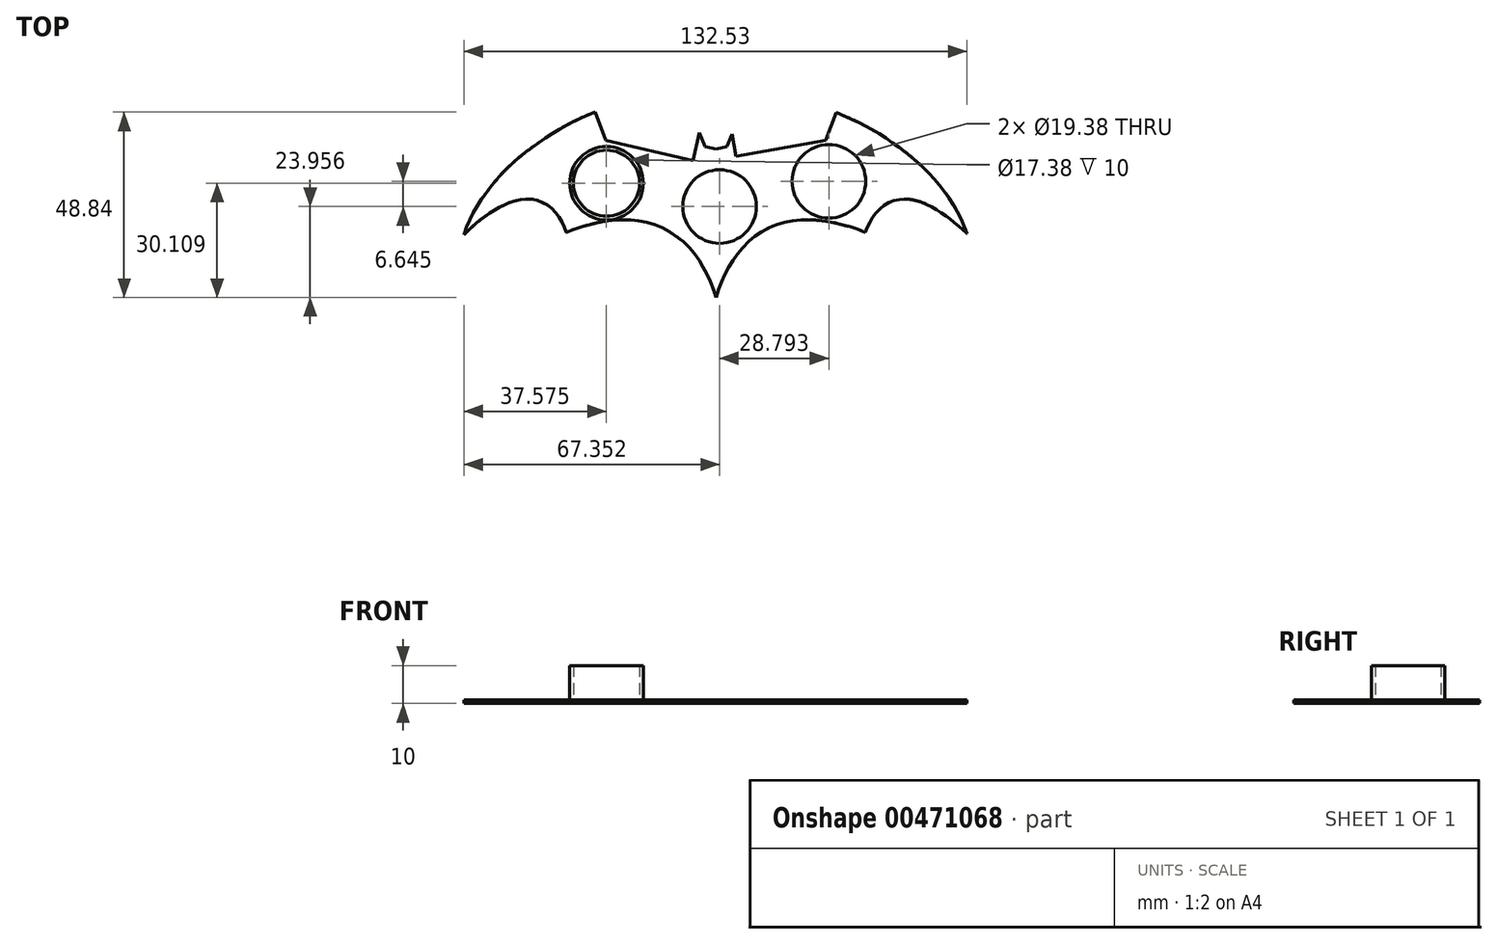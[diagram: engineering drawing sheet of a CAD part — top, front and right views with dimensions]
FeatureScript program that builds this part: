
annotation { "Feature Type Name" : "Feature", "Feature Type Description" : "" }
export const myFeature = defineFeature(function(context is Context, id is Id, definition is map)
    precondition{}
    {
        {
            var Q0;
            Q0=qCreatedBy(makeId("Top.planeOp"),FACE);
            var sketch = newSketch(context, id + "F0", { "sketchPlane" : qUnion([Q0])});
            skLineSegment(sketch, "E0", {"start": v(-31.58, 24.26) * mm, "end": v(-10.03, 19.27) * mm});
            skLineSegment(sketch, "E1", {"start": v(-8, 28.59) * mm, "end": v(-10.03, 19.27) * mm});
            skLineSegment(sketch, "E2", {"start": v(-8, 28.59) * mm, "end": v(-5.4, 22.6) * mm});
            skLineSegment(sketch, "E3", {"start": v(-5.4, 22.6) * mm, "end": v(-3.26, 22.12) * mm});
            skLineSegment(sketch, "E4", {"start": v(-3.26, 22.12) * mm, "end": v(-1.17, 22.6) * mm});
            skLineSegment(sketch, "E5", {"start": v(-1.17, 22.6) * mm, "end": v(1.35, 28.42) * mm});
            skLineSegment(sketch, "E6", {"start": v(1.35, 28.42) * mm, "end": v(2.82, 20.29) * mm});
            skLineSegment(sketch, "E7", {"start": v(2.82, 20.29) * mm, "end": v(24.86, 24.27) * mm});
            skLineSegment(sketch, "E8", {"start": v(24.86, 24.27) * mm, "end": v(27.86, 32.06) * mm});
            skLineSegment(sketch, "E9", {"start": v(-34.44, 32.06) * mm, "end": v(-31.58, 24.26) * mm});
            skFitSpline(sketch, "E10", {"points": [v(-71.54, -4.71) * mm, v(-71.03, -2.5) * mm, v(-69.95, 0.68) * mm, v(-67.87, 5.16) * mm, v(-64.53, 10.23) * mm, v(-59.84, 15.82) * mm, v(-53.37, 21.52) * mm, v(-43.46, 28) * mm, v(-34.44, 32.06) * mm], "startDerivative": vector(4.24, 29.82) * mm, "endDerivative": vector(55.88, 18.78) * mm});
            skFitSpline(sketch, "E11", {"points": [v(27.86, 32.06) * mm, v(37.3, 27.63) * mm, v(49.63, 19.06) * mm, v(56.76, 11.65) * mm, v(62.35, 2.73) * mm, v(64.86, -4.31) * mm, v(64.94, -4.74) * mm], "startDerivative": vector(44.14, -20.82) * mm, "endDerivative": vector(-0.74, -4.48) * mm});
            skFitSpline(sketch, "E12", {"points": [v(-3.32, -22.53) * mm, v(-2.72, -19.76) * mm, v(-1.9, -16.94) * mm, v(-0.8, -14.08) * mm, v(0.62, -11.17) * mm, v(2.24, -8.43) * mm, v(4.47, -5.7) * mm, v(6.98, -3.2) * mm, v(10.55, -0.92) * mm, v(13.84, 0.47) * mm, v(17.74, 1.21) * mm, v(20.5, 1.43) * mm, v(24.05, 1.25) * mm, v(27.15, 0.8) * mm, v(30.17, 0) * mm, v(32.95, -0.73) * mm, v(35, -1.57) * mm, v(36.1, -1.99) * mm, v(36.74, -2.23) * mm], "startDerivative": vector(8.47, 52.94) * mm, "endDerivative": vector(22.36, -9.6) * mm});
            skFitSpline(sketch, "E13", {"points": [v(36.74, -2.23) * mm, v(37.05, -1.12) * mm, v(37.6, 0.23) * mm, v(38.25, 1.59) * mm, v(39.23, 3.06) * mm, v(40.4, 4.38) * mm, v(41.46, 5.31) * mm, v(43.24, 6.28) * mm, v(44.9, 6.7) * mm, v(46.68, 6.86) * mm, v(48.66, 6.61) * mm, v(50.93, 5.93) * mm, v(52.85, 5.01) * mm, v(54.3, 4.22) * mm, v(56.14, 3) * mm, v(57.65, 1.91) * mm, v(59.33, 0.53) * mm, v(60.65, -0.55) * mm, v(62.13, -1.93) * mm, v(63.66, -3.41) * mm, v(64.95, -4.78) * mm, v(64.94, -4.74) * mm], "startDerivative": vector(6.9, 27.44) * mm, "endDerivative": vector(-2.9, -4.8) * mm});
            skFitSpline(sketch, "E14", {"points": [v(-43.33, -2.18) * mm, v(-41.74, -1.52) * mm, v(-38.77, -0.52) * mm, v(-35.27, 0.45) * mm, v(-31.24, 1.23) * mm, v(-28, 1.42) * mm, v(-24.68, 1.3) * mm, v(-21.72, 0.73) * mm, v(-19.2, 0) * mm, v(-16.85, -1.17) * mm, v(-14.55, -2.63) * mm, v(-12.25, -4.36) * mm, v(-10.35, -6.38) * mm, v(-8.73, -8.5) * mm, v(-6.94, -11.64) * mm, v(-5.72, -14.16) * mm, v(-4.63, -17.16) * mm, v(-3.93, -19.46) * mm, v(-3.32, -22.53) * mm], "startDerivative": vector(35.49, 10.52) * mm, "endDerivative": vector(12.6, -55.15) * mm});
            skFitSpline(sketch, "E15", {"points": [v(-71.54, -4.71) * mm, v(-70.46, -3.6) * mm, v(-68.76, -2.05) * mm, v(-66.86, -0.23) * mm, v(-65, 1.37) * mm, v(-62.35, 3.3) * mm, v(-60.63, 4.38) * mm, v(-58.87, 5.33) * mm, v(-57.1, 6.08) * mm, v(-55.15, 6.61) * mm, v(-53.48, 6.83) * mm, v(-51.43, 6.77) * mm, v(-50.1, 6.4) * mm, v(-48.82, 5.81) * mm, v(-47.8, 5.17) * mm, v(-46.87, 4.33) * mm, v(-46.13, 3.5) * mm, v(-45.4, 2.43) * mm, v(-44.7, 1.23) * mm, v(-44.2, 0.34) * mm, v(-43.79, -0.9) * mm, v(-43.47, -1.78) * mm, v(-43.33, -2.18) * mm], "startDerivative": vector(22.6, 24.07) * mm, "endDerivative": vector(5.32, -15.58) * mm});
            skCircle(sketch, "E16", {"center": v(26.46, 12.55) * mm, "radius": 8.7 * mm});
            skCircle(sketch, "E17", {"center": v(-2.34, 5.9) * mm, "radius": 8.7 * mm});
            skCircle(sketch, "E18", {"center": v(-32.12, 12.06) * mm, "radius": 8.7 * mm});
            skSolve(sketch);
        }
        {
            var Q0;
            Q0=makeQuery(id+"F0.imprint","IMPRINT",FACE,{"disambiguationData":[TD([[makeQuery(id+"F0.imprint","IMPRINT",EDGE,{"derivedFrom":sQuery(id+"F0.wireOp",EDGE,"E0")}),-1.0]])]});
            extrude(context, id + "F1", {"entities" : qUnion([Q0]), "depth" : 10 * mm});
        }
        {
            var Q0;
            Q0=makeQuery(id+"F1.opExtrude","CAP_FACE",FACE,{"disambiguationData":[OSD([sQuery(id+"F0.wireOp",EDGE,"E0"),sQuery(id+"F0.wireOp",EDGE,"E1"),sQuery(id+"F0.wireOp",EDGE,"E2"),sQuery(id+"F0.wireOp",EDGE,"E3"),sQuery(id+"F0.wireOp",EDGE,"E4"),sQuery(id+"F0.wireOp",EDGE,"E5"),sQuery(id+"F0.wireOp",EDGE,"E6"),sQuery(id+"F0.wireOp",EDGE,"E7"),sQuery(id+"F0.wireOp",EDGE,"E8"),sQuery(id+"F0.wireOp",EDGE,"E9"),sQuery(id+"F0.wireOp",EDGE,"E10"),sQuery(id+"F0.wireOp",EDGE,"E11"),sQuery(id+"F0.wireOp",EDGE,"E12"),sQuery(id+"F0.wireOp",EDGE,"E13"),sQuery(id+"F0.wireOp",EDGE,"E14"),sQuery(id+"F0.wireOp",EDGE,"E15")])],"isStart":false});
            shell(context, id + "F2", {"entities" : qUnion([Q0]), "thickness" : 1 * mm});
        }
        {
            var Q0;
            {var subQ0=sQuery(id+"F0.wireOp",EDGE,"E16");var subQ1=sQuery(id+"F0.wireOp",EDGE,"E15");var subQ2=sQuery(id+"F0.wireOp",EDGE,"E14");var subQ3=sQuery(id+"F0.wireOp",EDGE,"E13");var subQ4=sQuery(id+"F0.wireOp",EDGE,"E12");var subQ5=sQuery(id+"F0.wireOp",EDGE,"E11");var subQ6=sQuery(id+"F0.wireOp",EDGE,"E10");var subQ7=sQuery(id+"F0.wireOp",EDGE,"E9");var subQ8=sQuery(id+"F0.wireOp",EDGE,"E8");var subQ9=sQuery(id+"F0.wireOp",EDGE,"E7");var subQ10=sQuery(id+"F0.wireOp",EDGE,"E6");var subQ11=sQuery(id+"F0.wireOp",EDGE,"E5");var subQ12=sQuery(id+"F0.wireOp",EDGE,"E4");var subQ13=sQuery(id+"F0.wireOp",EDGE,"E3");var subQ14=sQuery(id+"F0.wireOp",EDGE,"E2");var subQ15=sQuery(id+"F0.wireOp",EDGE,"E1");var subQ16=sQuery(id+"F0.wireOp",EDGE,"E0");Q0=makeQuery(id+"F2.opShell","OFFSET_FACE",FACE,{"disambiguationData":[OSD([subQ16,subQ15,subQ14,subQ13,subQ12,subQ11,subQ10,subQ9,subQ8,subQ7,subQ6,subQ5,subQ4,subQ3,subQ2,subQ1,subQ0]),TDD([makeQuery(id+"F1.opExtrude","CAP_FACE",FACE,{"disambiguationData":[OSD([subQ16,subQ15,subQ14,subQ13,subQ12,subQ11,subQ10,subQ9,subQ8,subQ7,subQ6,subQ5,subQ4,subQ3,subQ2,subQ1,subQ0])],"isStart":false})])]});}
            var Q1;
            Q1=sQuery(id+"F0.wireOp",EDGE,"E16");
            extrude(context, id + "F3", {"entities" : qUnion([Q0]), "operationType" : NewBodyOperationType.REMOVE, "surfaceEntities" : qUnion([Q1]), "oppositeDirection" : true, "depth" : 25 * mm});
        }
    });
